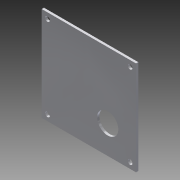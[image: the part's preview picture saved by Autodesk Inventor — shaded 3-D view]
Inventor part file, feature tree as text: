
AUTODESK INVENTOR PART (.ipt)
format: ipt  version: 2015 (Build 190159000, 159)  size: 98,304 bytes
history: native  units: in
note: dims shown in document units (in); Inventor stores cm internally (conversion verified against a paired STEP export)
features: other x5, sketch x1
ambient origin geometry x8: Origin, YZ Plane, XZ Plane, XY Plane, X Axis, Y Axis, Z Axis, Center Point
bodies: Solid1 (feature_tree)
feature tree (6):
  other  "gearboxbearingplate(gbpb).ipt"
  other  "Solid1::gearboxbearingplate(gbpb).ipt"
  other  "TaggingFeature1"
  sketch  "Sketch1"  dims[d0=0.3937in]
  other  "gbmh_sketch"
  other  "bearing_hole_sketch"
